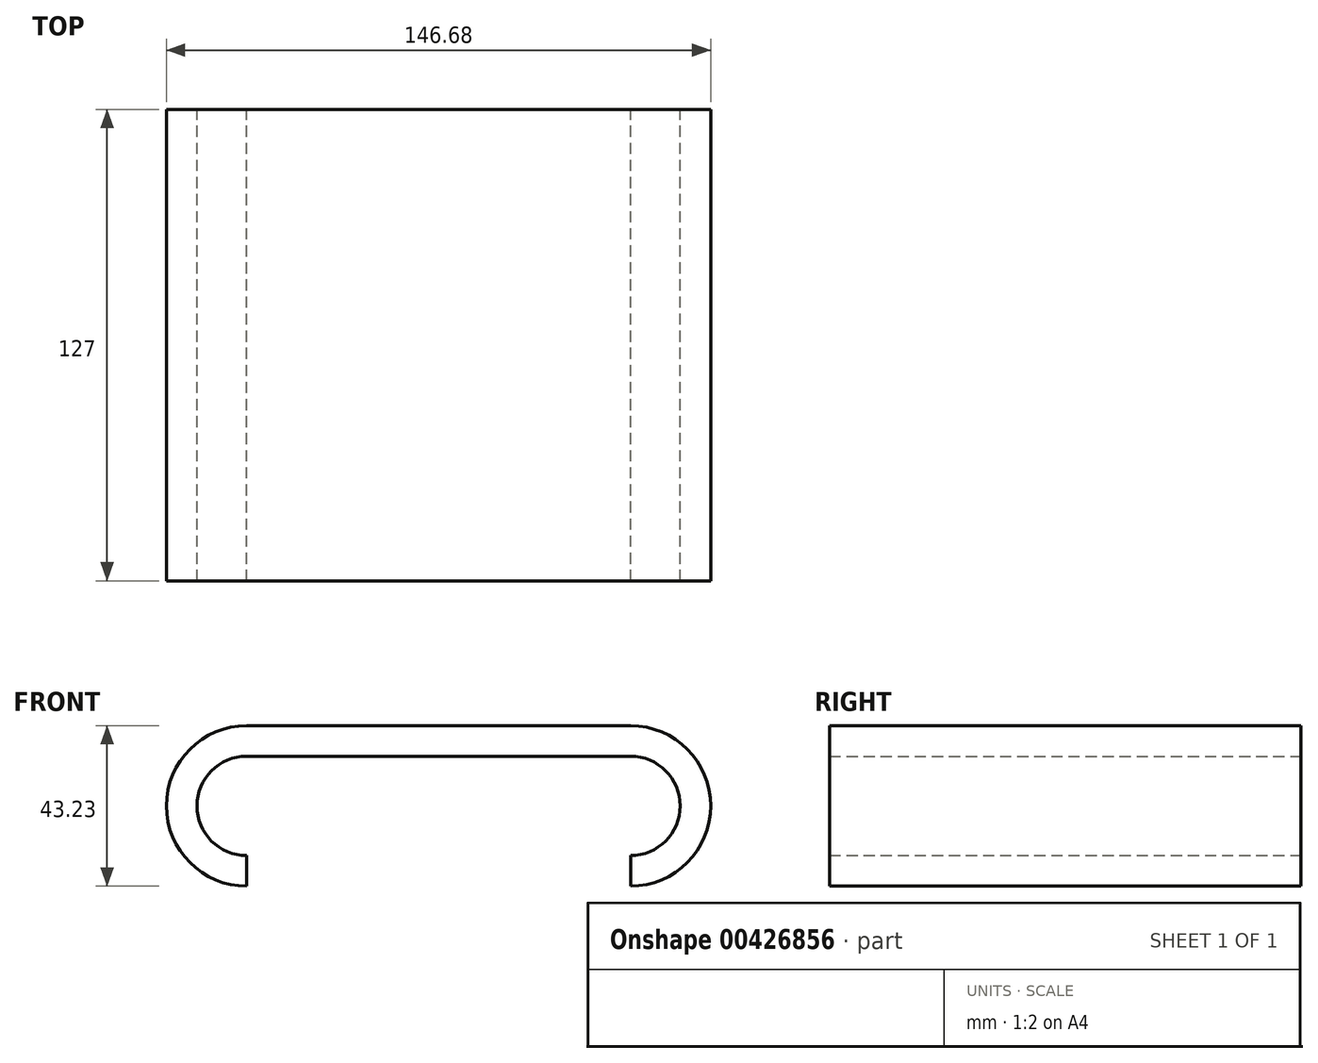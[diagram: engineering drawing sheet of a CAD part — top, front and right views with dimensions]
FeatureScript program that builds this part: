
annotation { "Feature Type Name" : "Feature", "Feature Type Description" : "" }
export const myFeature = defineFeature(function(context is Context, id is Id, definition is map)
    precondition{}
    {
        {
            var Q0;
            Q0=qCreatedBy(makeId("Front.planeOp"),FACE);
            var sketch = newSketch(context, id + "F0", { "sketchPlane" : qUnion([Q0])});
            skLineSegment(sketch, "E0.bottom", {"start": v(51.73, -4.12) * mm, "end": v(-51.73, -4.12) * mm});
            skLineSegment(sketch, "E0.top", {"start": v(51.73, 4.12) * mm, "end": v(-51.73, 4.12) * mm});
            skLineSegment(sketch, "E0.left", {"start": v(51.73, -4.12) * mm, "end": v(51.73, 4.12) * mm});
            skLineSegment(sketch, "E0.right", {"start": v(-51.73, -4.12) * mm, "end": v(-51.73, 4.12) * mm});
            skPoint(sketch, "E0.middle", {"position": v(0, 0) * mm});
            skLineSegment(sketch, "E1", {"start": v(-51.73, 4.12) * mm, "end": v(-51.73, -65.85) * mm, "construction": true});
            skPoint(sketch, "E1.endSnap0", {"position": v(-51.73, 0) * mm});
            skLineSegment(sketch, "E2", {"start": v(51.73, 4.12) * mm, "end": v(51.73, -59.78) * mm, "construction": true});
            skArc(sketch, "E3", {"start": v(-51.73, 4.12) * mm, "mid": v(-73.34, -17.5) * mm, "end": v(-51.73, -39.1) * mm});
            skPoint(sketch, "E3.first.point", {"position": v(-51.73, -39.1) * mm});
            skPoint(sketch, "E3.third.point", {"position": v(-30.35, -20.68) * mm});
            skArc(sketch, "E4", {"start": v(51.73, -39.1) * mm, "mid": v(73.34, -17.5) * mm, "end": v(51.73, 4.12) * mm});
            skPoint(sketch, "E4.first.point", {"position": v(51.73, -39.1) * mm});
            skPoint(sketch, "E4.third.point", {"position": v(64.42, 0) * mm});
            skPoint(sketch, "E4.third.point.positionSnap0", {"position": v(51.73, 0) * mm});
            skArc(sketch, "E5", {"start": v(-51.73, -4.12) * mm, "mid": v(-65.1, -17.5) * mm, "end": v(-51.73, -30.87) * mm});
            skArc(sketch, "E6", {"start": v(51.73, -30.87) * mm, "mid": v(65.1, -17.5) * mm, "end": v(51.73, -4.12) * mm});
            skLineSegment(sketch, "E7", {"start": v(-51.73, -30.87) * mm, "end": v(-51.73, -39.1) * mm});
            skLineSegment(sketch, "E8", {"start": v(51.73, -30.87) * mm, "end": v(51.73, -39.1) * mm});
            skSolve(sketch);
        }
        {
            var Q0;
            Q0 = qSketchRegion(id + "F0", true);
            extrude(context, id + "F1", {"entities" : qUnion([Q0]), "depth" : 127 * mm});
        }
    });
